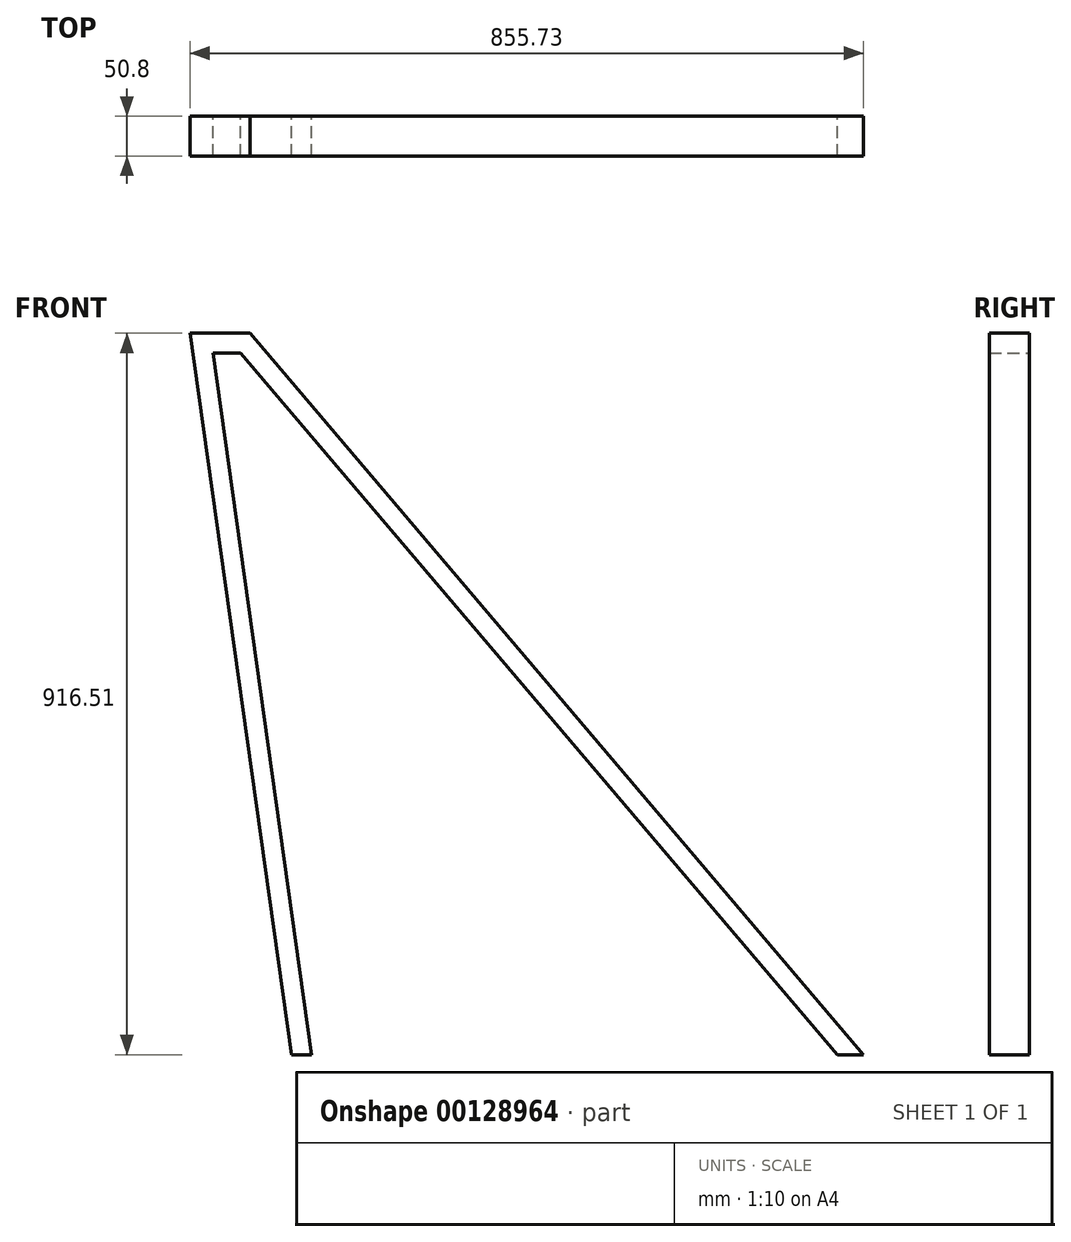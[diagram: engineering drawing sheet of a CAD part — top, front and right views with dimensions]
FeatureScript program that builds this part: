
annotation { "Feature Type Name" : "Feature", "Feature Type Description" : "" }
export const myFeature = defineFeature(function(context is Context, id is Id, definition is map)
    precondition{}
    {
        {
            var Q0;
            Q0=qCreatedBy(makeId("Front.planeOp"),FACE);
            var sketch = newSketch(context, id + "F0", { "sketchPlane" : qUnion([Q0])});
            skLineSegment(sketch, "E0", {"start": v(0, 0) * mm, "end": v(0, 914.4) * mm, "construction": true});
            skLineSegment(sketch, "E1", {"start": v(19.63, 774.7) * mm, "end": v(68.72, 425.45) * mm});
            skLineSegment(sketch, "E2", {"start": v(0, 914.4) * mm, "end": v(76.2, 914.4) * mm});
            skLineSegment(sketch, "E3", {"start": v(195.02, 774.7) * mm, "end": v(492.07, 425.45) * mm});
            skLineSegment(sketch, "E4", {"start": v(128.8, -2.11) * mm, "end": v(154.46, -2.11) * mm});
            skLineSegment(sketch, "E5.0", {"start": v(29.22, 889) * mm, "end": v(94.37, 425.45) * mm});
            skLineSegment(sketch, "E5.1", {"start": v(29.22, 889) * mm, "end": v(64.46, 889) * mm});
            skLineSegment(sketch, "E5.2", {"start": v(64.46, 889) * mm, "end": v(822.39, -2.11) * mm});
            skLineSegment(sketch, "E6.trimOffspring", {"start": v(822.39, -2.11) * mm, "end": v(855.73, -2.11) * mm});
            skLineSegment(sketch, "E7", {"start": v(-188.83, 914.4) * mm, "end": v(-188.83, 774.7) * mm, "construction": true});
            skLineSegment(sketch, "E8", {"start": v(-188.83, 774.7) * mm, "end": v(-188.83, 425.45) * mm, "construction": true});
            skLineSegment(sketch, "E9", {"start": v(-188.83, 425.45) * mm, "end": v(-188.83, 76.2) * mm, "construction": true});
            skLineSegment(sketch, "E10", {"start": v(-188.83, 76.2) * mm, "end": v(-188.83, 0) * mm, "construction": true});
            skLineSegment(sketch, "E11", {"start": v(-188.83, 774.7) * mm, "end": v(843.52, 774.7) * mm, "construction": true});
            skLineSegment(sketch, "E12", {"start": v(-188.83, 425.45) * mm, "end": v(843.52, 425.45) * mm, "construction": true});
            skLineSegment(sketch, "E13", {"start": v(-188.83, 76.2) * mm, "end": v(843.52, 76.2) * mm, "construction": true});
            skLineSegment(sketch, "E14", {"start": v(0, 914.4) * mm, "end": v(19.63, 774.7) * mm});
            skLineSegment(sketch, "E15.trimOffspring", {"start": v(117.8, 76.2) * mm, "end": v(128.8, -2.11) * mm});
            skLineSegment(sketch, "E16", {"start": v(68.72, 425.45) * mm, "end": v(117.8, 76.2) * mm});
            skLineSegment(sketch, "E17.trimOffspring", {"start": v(789.12, 76.2) * mm, "end": v(855.73, -2.11) * mm});
            skLineSegment(sketch, "E18", {"start": v(76.2, 914.4) * mm, "end": v(195.02, 774.7) * mm});
            skLineSegment(sketch, "E19", {"start": v(492.07, 425.45) * mm, "end": v(789.12, 76.2) * mm});
            skLineSegment(sketch, "E20", {"start": v(94.37, 425.45) * mm, "end": v(143.45, 76.2) * mm});
            skLineSegment(sketch, "E21", {"start": v(143.45, 76.2) * mm, "end": v(154.46, -2.11) * mm});
            skSolve(sketch);
        }
        {
            var Q0;
            Q0 = qSketchRegion(id + "F0", true);
            extrude(context, id + "F1", {"entities" : qUnion([Q0]), "depth" : 50.8 * mm});
        }
    });
